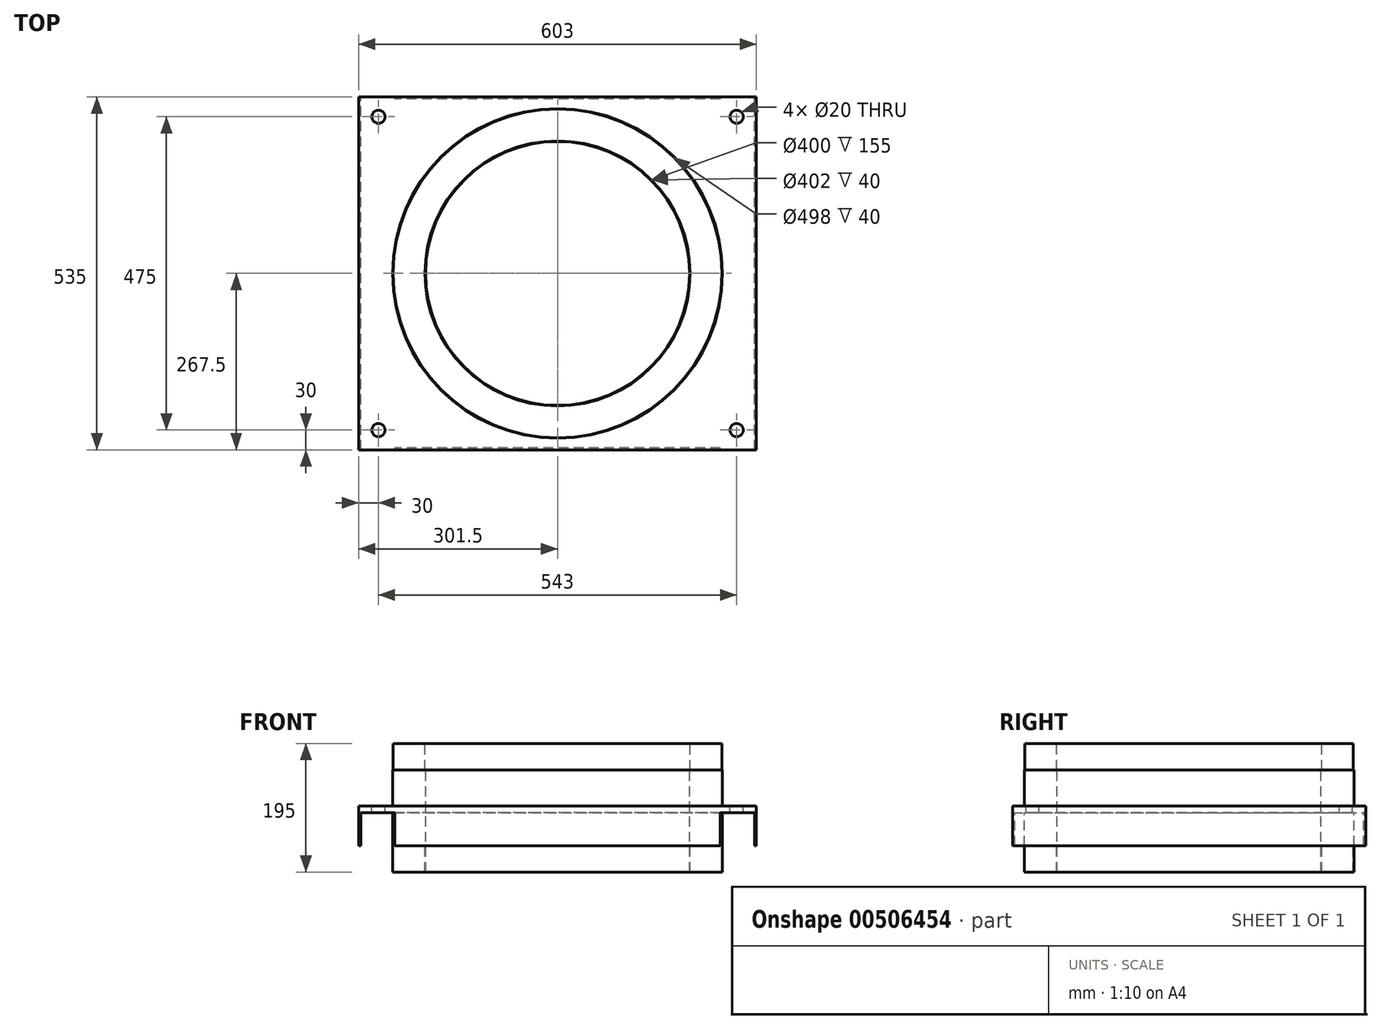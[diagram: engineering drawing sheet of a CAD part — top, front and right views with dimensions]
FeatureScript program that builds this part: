
annotation { "Feature Type Name" : "Feature", "Feature Type Description" : "" }
export const myFeature = defineFeature(function(context is Context, id is Id, definition is map)
    precondition{}
    {
        {
            var Q0;
            Q0=qCreatedBy(makeId("Front.planeOp"),FACE);
            var sketch = newSketch(context, id + "F0", { "sketchPlane" : qUnion([Q0])});
            skLineSegment(sketch, "E0", {"start": v(0, 74.87) * mm, "end": v(0, -73.71) * mm, "construction": true});
            skLineSegment(sketch, "E1", {"start": v(0, 374.84) * mm, "end": v(0, -528.94) * mm, "construction": true});
            skLineSegment(sketch, "E2", {"start": v(-200, -100) * mm, "end": v(-200, 55) * mm});
            skLineSegment(sketch, "E3", {"start": v(-200, 55) * mm, "end": v(-201, 55) * mm});
            skLineSegment(sketch, "E4", {"start": v(-201, 55) * mm, "end": v(-201, 95) * mm});
            skLineSegment(sketch, "E5", {"start": v(-201, 95) * mm, "end": v(-249, 95) * mm});
            skLineSegment(sketch, "E6", {"start": v(-249, 95) * mm, "end": v(-249, 55) * mm});
            skLineSegment(sketch, "E7", {"start": v(-249, 55) * mm, "end": v(-250, 55) * mm});
            skLineSegment(sketch, "E8", {"start": v(-250, 55) * mm, "end": v(-250, -100) * mm});
            skLineSegment(sketch, "E9", {"start": v(-250, -100) * mm, "end": v(-249, -100) * mm});
            skLineSegment(sketch, "E10", {"start": v(-249, -100) * mm, "end": v(-249, -60) * mm});
            skLineSegment(sketch, "E11", {"start": v(-249, -60) * mm, "end": v(-201, -60) * mm});
            skLineSegment(sketch, "E12", {"start": v(-201, -60) * mm, "end": v(-201, -100) * mm});
            skLineSegment(sketch, "E13", {"start": v(-201, -100) * mm, "end": v(-200, -100) * mm});
            skSolve(sketch);
        }
        {
            var Q0;
            Q0=qSketchRegion(id+"F0",true);
            var Q1;
            Q1=sQuery(id+"F0.wireOp",EDGE,"E1");
            revolve(context, id + "F1", {"entities" : qUnion([Q0]), "axis" : qUnion([Q1]), "revolveType" : RevolveType.FULL});
        }
        {
            var Q0;
            Q0=qCreatedBy(makeId("Top.planeOp"),FACE);
            var sketch = newSketch(context, id + "F2", { "sketchPlane" : qUnion([Q0])});
            skLineSegment(sketch, "E14.bottom", {"start": v(301.5, 267.5) * mm, "end": v(-301.5, 267.5) * mm});
            skLineSegment(sketch, "E14.top", {"start": v(301.5, -267.5) * mm, "end": v(-301.5, -267.5) * mm});
            skLineSegment(sketch, "E14.left", {"start": v(301.5, 267.5) * mm, "end": v(301.5, -267.5) * mm});
            skLineSegment(sketch, "E14.right", {"start": v(-301.5, 267.5) * mm, "end": v(-301.5, -267.5) * mm});
            skPoint(sketch, "E14.middle", {"position": v(0, 0) * mm});
            skCircle(sketch, "E15.0", {"center": v(0, 0) * mm, "radius": 201 * mm});
            skCircle(sketch, "E16.0", {"center": v(0, 0) * mm, "radius": 200 * mm});
            skLineSegment(sketch, "E17", {"start": v(0, 0) * mm, "end": v(0, 773.78) * mm, "construction": true});
            skLineSegment(sketch, "E18", {"start": v(0, 0) * mm, "end": v(1007.48, 0) * mm, "construction": true});
            skCircle(sketch, "E19", {"center": v(271.5, 237.5) * mm, "radius": 10 * mm});
            skCircle(sketch, "E20.MirrorC", {"center": v(-271.5, 237.5) * mm, "radius": 10 * mm});
            skCircle(sketch, "E21.MirrorC", {"center": v(271.5, -237.5) * mm, "radius": 10 * mm});
            skCircle(sketch, "E22.MirrorC", {"center": v(-271.5, -237.5) * mm, "radius": 10 * mm});
            skSolve(sketch);
        }
        {
            var Q0;
            Q0=qSketchRegion(id+"F2",true);
            extrude(context, id + "F3", {"entities" : qUnion([Q0]), "operationType" : NewBodyOperationType.ADD, "oppositeDirection" : true, "depth" : 10 * mm});
        }
        {
            var Q0;
            Q0=makeQuery(id+"F3.opExtrude","CAP_FACE",FACE,{"disambiguationData":[OSD([sQuery(id+"F2.wireOp",EDGE,"E14.bottom"),sQuery(id+"F2.wireOp",EDGE,"E14.top"),sQuery(id+"F2.wireOp",EDGE,"E14.left"),sQuery(id+"F2.wireOp",EDGE,"E14.right"),sQuery(id+"F2.wireOp",EDGE,"E16.0"),sQuery(id+"F2.wireOp",EDGE,"E19"),sQuery(id+"F2.wireOp",EDGE,"E20.MirrorC"),sQuery(id+"F2.wireOp",EDGE,"E21.MirrorC"),sQuery(id+"F2.wireOp",EDGE,"E22.MirrorC")])],"isStart":false});
            var sketch = newSketch(context, id + "F4", { "sketchPlane" : qUnion([Q0])});
            skLineSegment(sketch, "E23", {"start": v(0, 0) * mm, "end": v(-1098.02, 0) * mm, "construction": true});
            skLineSegment(sketch, "E24", {"start": v(0, 0) * mm, "end": v(0, -1084.2) * mm, "construction": true});
            skLineSegment(sketch, "E25.bottom", {"start": v(246.5, 267.5) * mm, "end": v(-246.5, 267.5) * mm});
            skLineSegment(sketch, "E25.top", {"start": v(246.5, 264.5) * mm, "end": v(-246.5, 264.5) * mm});
            skLineSegment(sketch, "E25.left", {"start": v(246.5, 267.5) * mm, "end": v(246.5, 264.5) * mm});
            skLineSegment(sketch, "E25.right", {"start": v(-246.5, 267.5) * mm, "end": v(-246.5, 264.5) * mm});
            skLineSegment(sketch, "E26.bottom", {"start": v(-301.5, 267.5) * mm, "end": v(-298.5, 267.5) * mm});
            skLineSegment(sketch, "E26.top", {"start": v(-301.5, -267.5) * mm, "end": v(-298.5, -267.5) * mm});
            skLineSegment(sketch, "E26.left", {"start": v(-301.5, 267.5) * mm, "end": v(-301.5, -267.5) * mm});
            skLineSegment(sketch, "E26.right", {"start": v(-298.5, 267.5) * mm, "end": v(-298.5, -267.5) * mm});
            skLineSegment(sketch, "E27.MirrorCS", {"start": v(246.5, -267.5) * mm, "end": v(246.5, -264.5) * mm});
            skLineSegment(sketch, "E28.MirrorCS", {"start": v(-246.5, -267.5) * mm, "end": v(-246.5, -264.5) * mm});
            skLineSegment(sketch, "E29.MirrorCS", {"start": v(246.5, -264.5) * mm, "end": v(-246.5, -264.5) * mm});
            skLineSegment(sketch, "E30.MirrorCS", {"start": v(246.5, -267.5) * mm, "end": v(-246.5, -267.5) * mm});
            skLineSegment(sketch, "E31.MirrorCS", {"start": v(301.5, -267.5) * mm, "end": v(298.5, -267.5) * mm});
            skLineSegment(sketch, "E32.MirrorCS", {"start": v(301.5, 267.5) * mm, "end": v(298.5, 267.5) * mm});
            skLineSegment(sketch, "E33.MirrorCS", {"start": v(301.5, 267.5) * mm, "end": v(301.5, -267.5) * mm});
            skLineSegment(sketch, "E34.MirrorCS", {"start": v(298.5, 267.5) * mm, "end": v(298.5, -267.5) * mm});
            skLineSegment(sketch, "E35.MirrorCS", {"start": v(0, 0) * mm, "end": v(1098.02, 0) * mm, "construction": true});
            skSolve(sketch);
        }
        {
            var Q0;
            Q0=qSketchRegion(id+"F4",true);
            extrude(context, id + "F5", {"entities" : qUnion([Q0]), "operationType" : NewBodyOperationType.ADD, "depth" : 50 * mm});
        }
    });
